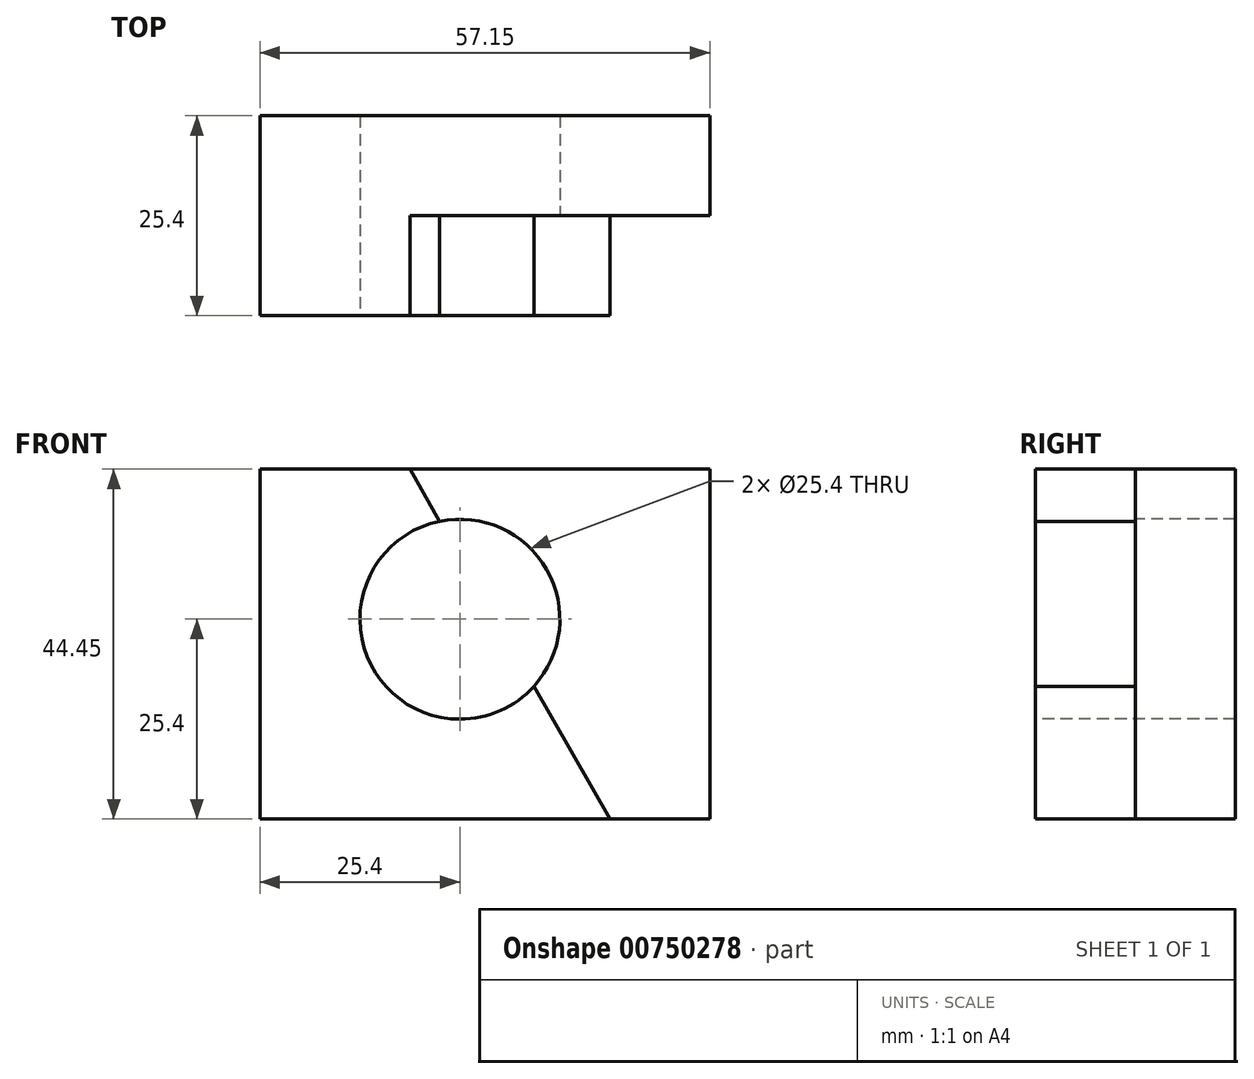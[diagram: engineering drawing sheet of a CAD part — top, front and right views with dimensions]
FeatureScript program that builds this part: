
annotation { "Feature Type Name" : "Feature", "Feature Type Description" : "" }
export const myFeature = defineFeature(function(context is Context, id is Id, definition is map)
    precondition{}
    {
        {
            var Q0;
            Q0=qCreatedBy(makeId("Front.planeOp"),FACE);
            var sketch = newSketch(context, id + "F0", { "sketchPlane" : qUnion([Q0])});
            skLineSegment(sketch, "E0.bottom", {"start": v(0, 0) * mm, "end": v(57.15, 0) * mm});
            skLineSegment(sketch, "E0.top", {"start": v(0, 44.45) * mm, "end": v(57.15, 44.45) * mm});
            skLineSegment(sketch, "E0.left", {"start": v(0, 0) * mm, "end": v(0, 44.45) * mm});
            skLineSegment(sketch, "E0.right", {"start": v(57.15, 0) * mm, "end": v(57.15, 44.45) * mm});
            skSolve(sketch);
        }
        {
            var Q0;
            Q0=makeQuery(id+"F0.imprint","IMPRINT",FACE,{"disambiguationData":[TD([[makeQuery(id+"F0.imprint","IMPRINT",EDGE,{"derivedFrom":sQuery(id+"F0.wireOp",EDGE,"E0.bottom")}),1.0]])]});
            extrude(context, id + "F1", {"entities" : qUnion([Q0]), "depth" : 25.4 * mm, "offsetDistance" : 25.4 * mm});
        }
        {
            var Q0;
            Q0=makeQuery(id+"F1.opExtrude","CAP_FACE",FACE,{"disambiguationData":[OSD([sQuery(id+"F0.wireOp",EDGE,"E0.bottom"),sQuery(id+"F0.wireOp",EDGE,"E0.top"),sQuery(id+"F0.wireOp",EDGE,"E0.left"),sQuery(id+"F0.wireOp",EDGE,"E0.right")])],"isStart":false});
            var sketch = newSketch(context, id + "F2", { "sketchPlane" : qUnion([Q0])});
            skLineSegment(sketch, "E1", {"start": v(19.05, 44.45) * mm, "end": v(44.45, 0) * mm});
            skCircle(sketch, "E2", {"center": v(25.4, 25.4) * mm, "radius": 12.7 * mm});
            skSolve(sketch);
        }
        {
            var Q0;
            {var subQ0=makeQuery(id+"F1.opExtrude","CAP_EDGE",EDGE,{"disambiguationData":[OSD([sQuery(id+"F0.wireOp",EDGE,"E0.right")])],"isStart":false});Q0=makeQuery(id+"F2.imprint","IMPRINT",FACE,{"disambiguationData":[TD([[makeQuery(id+"F2.imprint","IMPRINT",EDGE,{"derivedFrom":subQ0}),1.0]])]});}
            extrude(context, id + "F3", {"entities" : qUnion([Q0]), "operationType" : NewBodyOperationType.REMOVE, "oppositeDirection" : true, "depth" : 12.7 * mm, "offsetDistance" : 25.4 * mm});
        }
        {
            var Q0;
            {var subQ0=sQuery(id+"F2.wireOp",EDGE,"E2");var subQ1=sQuery(id+"F2.wireOp",EDGE,"E1");var subQ2=makeQuery(id+"F2.imprint","INTERSECT",VERTEX,{"disambiguationData":[OD(0.0)],"derivedFrom":[subQ1,subQ0]});Q0=makeQuery(id+"F2.imprint","IMPRINT",FACE,{"disambiguationData":[TD([[makeQuery(id+"F2.imprint","IMPRINT",EDGE,{"disambiguationData":[TD([[subQ2,-1.0]])],"derivedFrom":subQ1}),-1.0]])]});}
            var Q1;
            {var subQ0=sQuery(id+"F2.wireOp",EDGE,"E2");var subQ1=sQuery(id+"F2.wireOp",EDGE,"E1");var subQ2=makeQuery(id+"F2.imprint","INTERSECT",VERTEX,{"disambiguationData":[OD(0.0)],"derivedFrom":[subQ1,subQ0]});Q1=makeQuery(id+"F2.imprint","IMPRINT",FACE,{"disambiguationData":[TD([[makeQuery(id+"F2.imprint","IMPRINT",EDGE,{"disambiguationData":[TD([[subQ2,-1.0]])],"derivedFrom":subQ1}),1.0]])]});}
            extrude(context, id + "F4", {"entities" : qUnion([Q0, Q1]), "operationType" : NewBodyOperationType.REMOVE, "oppositeDirection" : true, "depth" : 25.4 * mm, "offsetDistance" : 25.4 * mm});
        }
    });
